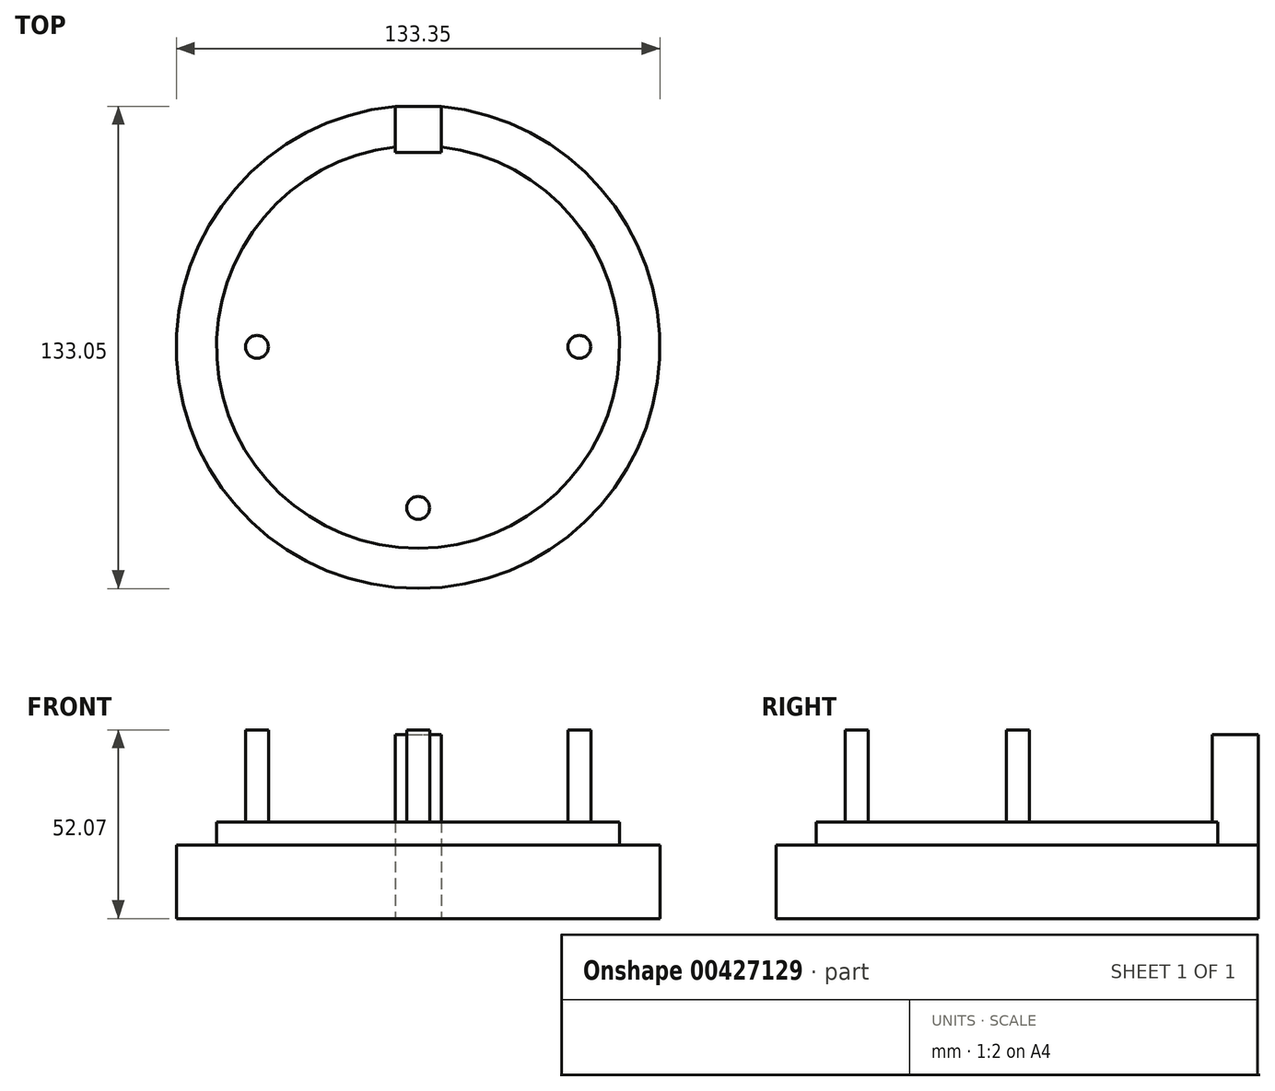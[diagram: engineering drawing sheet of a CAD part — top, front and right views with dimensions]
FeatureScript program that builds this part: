
annotation { "Feature Type Name" : "Feature", "Feature Type Description" : "" }
export const myFeature = defineFeature(function(context is Context, id is Id, definition is map)
    precondition{}
    {
        {
            var Q0;
            Q0=qCreatedBy(makeId("Top.planeOp"),FACE);
            var sketch = newSketch(context, id + "F0", { "sketchPlane" : qUnion([Q0])});
            skArc(sketch, "E0", {"start": v(-6.35, 66.37) * mm, "mid": v(0, -66.68) * mm, "end": v(6.35, 66.37) * mm});
            skLineSegment(sketch, "E1.top", {"start": v(-6.35, 53.67) * mm, "end": v(6.35, 53.67) * mm});
            skLineSegment(sketch, "E1.left", {"start": v(-6.35, 66.37) * mm, "end": v(-6.35, 53.67) * mm});
            skLineSegment(sketch, "E1.right", {"start": v(6.35, 66.37) * mm, "end": v(6.35, 53.67) * mm});
            skSolve(sketch);
        }
        {
            var Q0;
            Q0 = qSketchRegion(id + "F0", true);
            extrude(context, id + "F1", {"entities" : qUnion([Q0]), "depth" : 20.32 * mm});
        }
        {
            var Q0;
            Q0=makeQuery(id+"F1.opExtrude","CAP_FACE",FACE,{"disambiguationData":[OSD([sQuery(id+"F0.wireOp",EDGE,"E0"),sQuery(id+"F0.wireOp",EDGE,"E1.top"),sQuery(id+"F0.wireOp",EDGE,"E1.left"),sQuery(id+"F0.wireOp",EDGE,"E1.right")])],"isStart":false});
            var sketch = newSketch(context, id + "F2", { "sketchPlane" : qUnion([Q0])});
            skArc(sketch, "E2", {"start": v(-6.35, 55.2) * mm, "mid": v(0, -55.56) * mm, "end": v(6.35, 55.2) * mm});
            skLineSegment(sketch, "E3.0", {"start": v(-6.35, 55.2) * mm, "end": v(-6.35, 53.67) * mm});
            skLineSegment(sketch, "E4.0", {"start": v(6.35, 55.2) * mm, "end": v(6.35, 53.67) * mm});
            skLineSegment(sketch, "E5.0", {"start": v(-6.35, 53.67) * mm, "end": v(6.35, 53.67) * mm});
            skPoint(sketch, "E6.orphan", {"position": v(-6.35, 66.37) * mm});
            skPoint(sketch, "E7.orphan", {"position": v(6.35, 66.37) * mm});
            skSolve(sketch);
        }
        {
            var Q0;
            Q0 = qSketchRegion(id + "F2", true);
            extrude(context, id + "F3", {"entities" : qUnion([Q0]), "operationType" : NewBodyOperationType.ADD, "depth" : 6.35 * mm});
        }
        {
            var Q0;
            Q0=qCreatedBy(makeId("Top.planeOp"),FACE);
            var sketch = newSketch(context, id + "F4", { "sketchPlane" : qUnion([Q0])});
            skLineSegment(sketch, "E8.0", {"start": v(-6.35, 53.67) * mm, "end": v(6.35, 53.67) * mm});
            skLineSegment(sketch, "E9.0", {"start": v(-6.35, 55.2) * mm, "end": v(-6.35, 53.67) * mm});
            skLineSegment(sketch, "E10.0", {"start": v(-6.35, 66.37) * mm, "end": v(-6.35, 55.2) * mm});
            skLineSegment(sketch, "E11.top", {"start": v(-6.35, 66.37) * mm, "end": v(6.35, 66.37) * mm});
            skLineSegment(sketch, "E11.left", {"start": v(-6.35, 53.67) * mm, "end": v(-6.35, 66.37) * mm});
            skLineSegment(sketch, "E11.right", {"start": v(6.35, 53.67) * mm, "end": v(6.35, 66.37) * mm});
            skSolve(sketch);
        }
        {
            var Q0;
            Q0 = qSketchRegion(id + "F4", true);
            extrude(context, id + "F5", {"entities" : qUnion([Q0]), "operationType" : NewBodyOperationType.ADD, "depth" : 50.8 * mm});
        }
        {
            var Q0;
            Q0=makeQuery(id+"F3.opExtrude","CAP_FACE",FACE,{"disambiguationData":[OSD([sQuery(id+"F2.wireOp",EDGE,"E2"),sQuery(id+"F2.wireOp",EDGE,"E3.0"),sQuery(id+"F2.wireOp",EDGE,"E4.0"),sQuery(id+"F2.wireOp",EDGE,"E5.0")])],"isStart":false});
            var sketch = newSketch(context, id + "F6", { "sketchPlane" : qUnion([Q0])});
            skCircle(sketch, "E12", {"center": v(0, 0) * mm, "radius": 63.5 * mm});
            skCircle(sketch, "E13", {"center": v(0, -44.45) * mm, "radius": 3.18 * mm});
            skCircle(sketch, "E14.1.1", {"center": v(44.45, 0) * mm, "radius": 3.18 * mm});
            skCircle(sketch, "E14.3.1", {"center": v(-44.45, 0) * mm, "radius": 3.18 * mm});
            skSolve(sketch);
        }
        {
            var Q0;
            Q0=makeQuery(id+"F6.imprint","IMPRINT",FACE,{"disambiguationData":[TD([[makeQuery(id+"F6.imprint","IMPRINT",EDGE,{"derivedFrom":sQuery(id+"F6.wireOp",EDGE,"E14.1.1")}),1.0]])]});
            var Q1;
            Q1=makeQuery(id+"F6.imprint","IMPRINT",FACE,{"disambiguationData":[TD([[makeQuery(id+"F6.imprint","IMPRINT",EDGE,{"derivedFrom":sQuery(id+"F6.wireOp",EDGE,"E13")}),1.0]])]});
            var Q2;
            Q2=makeQuery(id+"F6.imprint","IMPRINT",FACE,{"disambiguationData":[TD([[makeQuery(id+"F6.imprint","IMPRINT",EDGE,{"derivedFrom":sQuery(id+"F6.wireOp",EDGE,"E14.3.1")}),1.0]])]});
            extrude(context, id + "F7", {"entities" : qUnion([Q0, Q1, Q2]), "operationType" : NewBodyOperationType.ADD, "depth" : 25.4 * mm});
        }
    });
